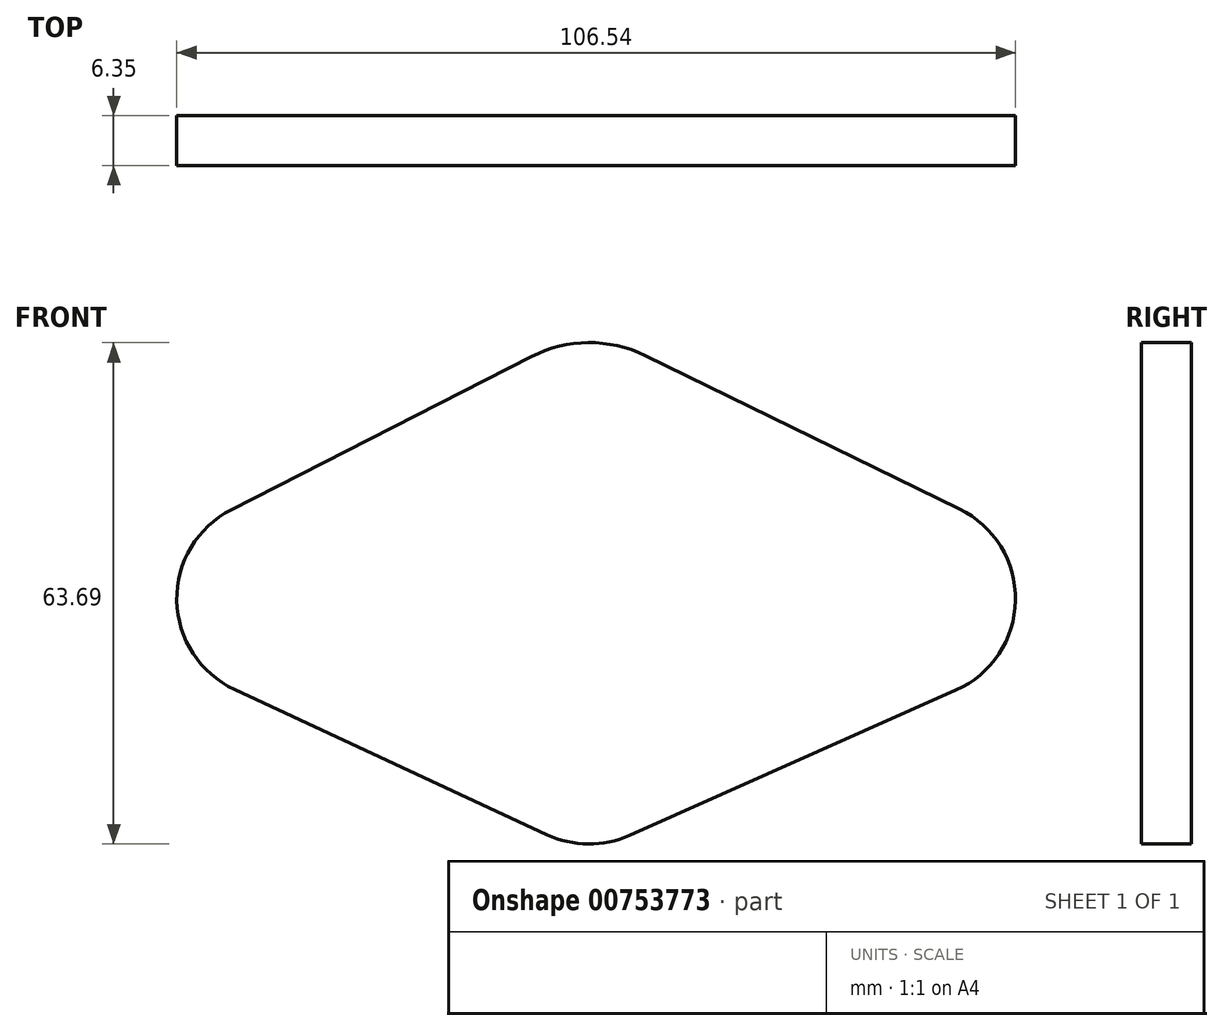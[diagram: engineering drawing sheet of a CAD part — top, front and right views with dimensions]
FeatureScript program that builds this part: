
annotation { "Feature Type Name" : "Feature", "Feature Type Description" : "" }
export const myFeature = defineFeature(function(context is Context, id is Id, definition is map)
    precondition{}
    {
        {
            var Q0;
            Q0=qCreatedBy(makeId("Front.planeOp"),FACE);
            var sketch = newSketch(context, id + "F0", { "sketchPlane" : qUnion([Q0])});
            skLineSegment(sketch, "E0", {"start": v(-45.32, 11.84) * mm, "end": v(-7.18, 31.3) * mm});
            skLineSegment(sketch, "E1", {"start": v(7.25, 31.43) * mm, "end": v(47.16, 11.95) * mm});
            skLineSegment(sketch, "E2", {"start": v(-44.9, -10.99) * mm, "end": v(-5.24, -29.44) * mm});
            skLineSegment(sketch, "E3", {"start": v(5.28, -29.53) * mm, "end": v(46.75, -11.07) * mm});
            skPoint(sketch, "E4.visualSharp", {"position": v(0, 34.97) * mm});
            skArc(sketch, "E4.filletArc", {"start": v(7.25, 31.43) * mm, "mid": v(0.02, 33.07) * mm, "end": v(-7.18, 31.3) * mm});
            skPoint(sketch, "E5.visualSharp", {"position": v(0, -31.87) * mm});
            skArc(sketch, "E5.filletArc", {"start": v(-5.24, -29.44) * mm, "mid": v(0.01, -30.62) * mm, "end": v(5.28, -29.53) * mm});
            skPoint(sketch, "E6.visualSharp", {"position": v(71.62, 0) * mm});
            skArc(sketch, "E6.filletArc", {"start": v(46.75, -11.07) * mm, "mid": v(54.28, 0.3) * mm, "end": v(47.16, 11.95) * mm});
            skPoint(sketch, "E7.visualSharp", {"position": v(-68.52, 0) * mm});
            skArc(sketch, "E7.filletArc", {"start": v(-45.32, 11.84) * mm, "mid": v(-52.25, 0.3) * mm, "end": v(-44.9, -10.99) * mm});
            skSolve(sketch);
        }
        {
            var Q0;
            Q0=makeQuery(id+"F0.imprint","IMPRINT",FACE,{"disambiguationData":[TD([[makeQuery(id+"F0.imprint","IMPRINT",EDGE,{"derivedFrom":sQuery(id+"F0.wireOp",EDGE,"E0")}),-1.0]])]});
            extrude(context, id + "F1", {"entities" : qUnion([Q0]), "depth" : 6.35 * mm, "offsetDistance" : 25.4 * mm});
        }
    });
